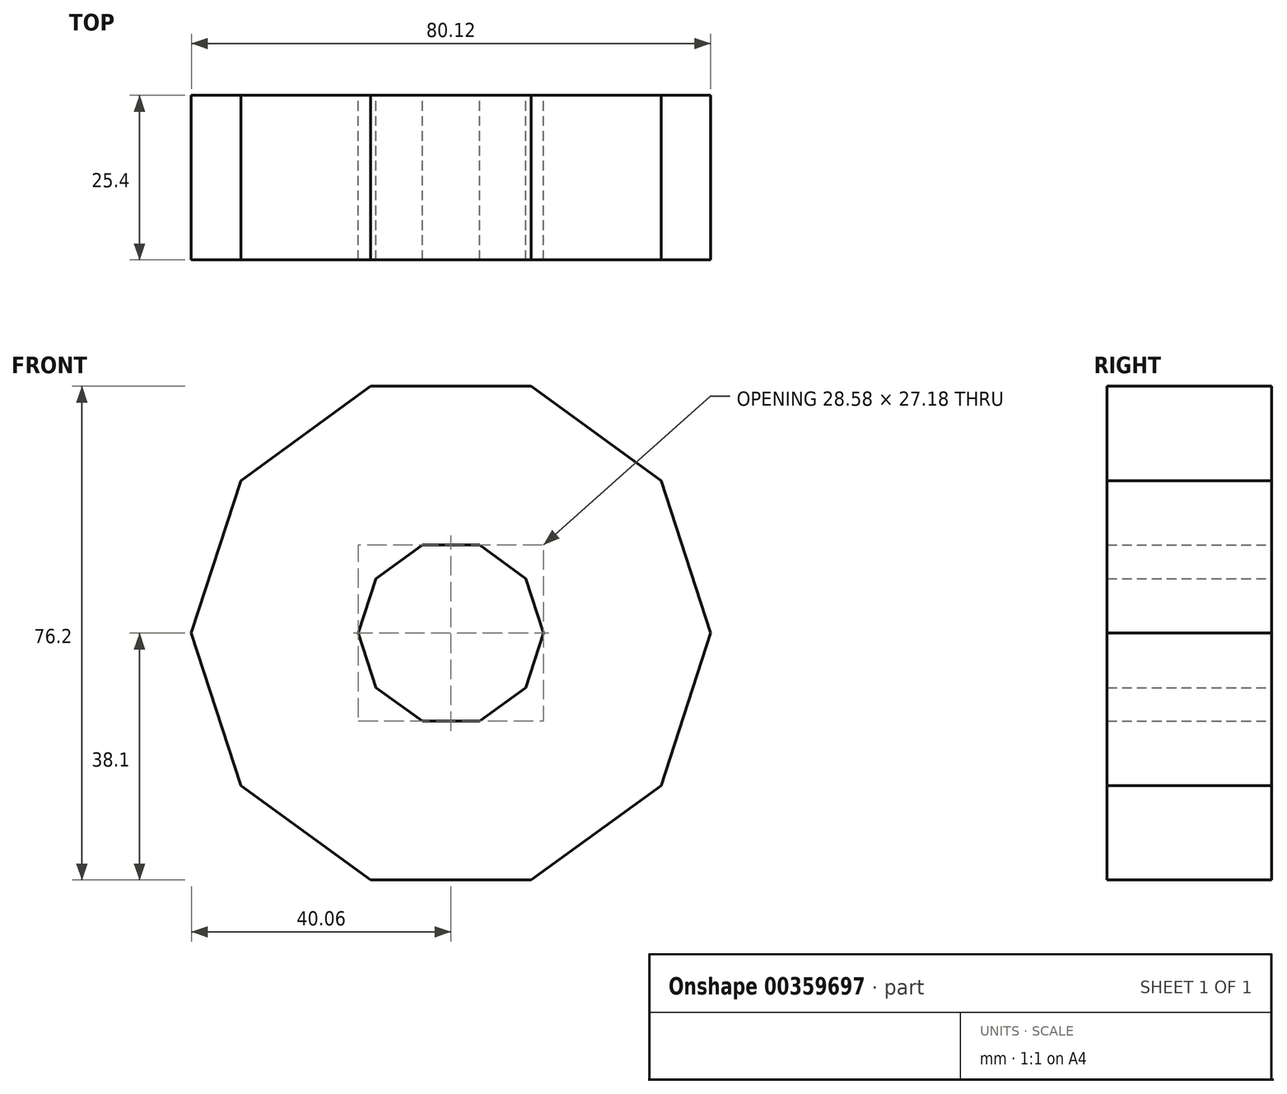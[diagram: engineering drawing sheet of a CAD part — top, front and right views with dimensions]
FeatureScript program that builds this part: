
annotation { "Feature Type Name" : "Feature", "Feature Type Description" : "" }
export const myFeature = defineFeature(function(context is Context, id is Id, definition is map)
    precondition{}
    {
        {
            var Q0;
            Q0=qCreatedBy(makeId("Front.planeOp"),FACE);
            var sketch = newSketch(context, id + "F0", { "sketchPlane" : qUnion([Q0])});
            skLineSegment(sketch, "E0", {"start": v(0, 0) * mm, "end": v(0, 38.1) * mm});
            skLineSegment(sketch, "E1", {"start": v(0, 0) * mm, "end": v(0, 13.59) * mm});
            skCircle(sketch, "E2.cCircle", {"center": v(0, 0) * mm, "radius": 38.1 * mm, "construction": true});
            skLineSegment(sketch, "E2.0", {"start": v(-12.38, 38.1) * mm, "end": v(12.38, 38.1) * mm});
            skLineSegment(sketch, "E2.1", {"start": v(12.38, 38.1) * mm, "end": v(32.4, 23.55) * mm});
            skLineSegment(sketch, "E2.2", {"start": v(32.4, 23.55) * mm, "end": v(40.06, 0) * mm});
            skLineSegment(sketch, "E2.3", {"start": v(40.06, 0) * mm, "end": v(32.4, -23.55) * mm});
            skLineSegment(sketch, "E2.4", {"start": v(32.4, -23.55) * mm, "end": v(12.38, -38.1) * mm});
            skLineSegment(sketch, "E2.5", {"start": v(12.38, -38.1) * mm, "end": v(-12.38, -38.1) * mm});
            skLineSegment(sketch, "E2.6", {"start": v(-12.38, -38.1) * mm, "end": v(-32.4, -23.55) * mm});
            skLineSegment(sketch, "E2.7", {"start": v(-32.4, -23.55) * mm, "end": v(-40.06, 0) * mm});
            skLineSegment(sketch, "E2.8", {"start": v(-40.06, 0) * mm, "end": v(-32.4, 23.55) * mm});
            skLineSegment(sketch, "E2.9", {"start": v(-32.4, 23.55) * mm, "end": v(-12.38, 38.1) * mm});
            skPoint(sketch, "E2.0.midPoint", {"position": v(0, 38.1) * mm});
            skCircle(sketch, "E3.cCircle", {"center": v(0, 0) * mm, "radius": 13.59 * mm, "construction": true});
            skLineSegment(sketch, "E3.0", {"start": v(-4.42, 13.59) * mm, "end": v(4.42, 13.59) * mm});
            skLineSegment(sketch, "E3.1", {"start": v(4.42, 13.59) * mm, "end": v(11.56, 8.4) * mm});
            skLineSegment(sketch, "E3.2", {"start": v(11.56, 8.4) * mm, "end": v(14.29, 0) * mm});
            skLineSegment(sketch, "E3.3", {"start": v(14.29, 0) * mm, "end": v(11.56, -8.4) * mm});
            skLineSegment(sketch, "E3.4", {"start": v(11.56, -8.4) * mm, "end": v(4.42, -13.59) * mm});
            skLineSegment(sketch, "E3.5", {"start": v(4.42, -13.59) * mm, "end": v(-4.42, -13.59) * mm});
            skLineSegment(sketch, "E3.6", {"start": v(-4.42, -13.59) * mm, "end": v(-11.56, -8.4) * mm});
            skLineSegment(sketch, "E3.7", {"start": v(-11.56, -8.4) * mm, "end": v(-14.29, 0) * mm});
            skLineSegment(sketch, "E3.8", {"start": v(-14.29, 0) * mm, "end": v(-11.56, 8.4) * mm});
            skLineSegment(sketch, "E3.9", {"start": v(-11.56, 8.4) * mm, "end": v(-4.42, 13.59) * mm});
            skPoint(sketch, "E3.0.midPoint", {"position": v(0, 13.59) * mm});
            skSolve(sketch);
        }
        {
            var Q0;
            {var subQ3=sQuery(id+"F0.wireOp",EDGE,"E2.1");Q0=makeQuery(id+"F0.imprint","IMPRINT",FACE,{"disambiguationData":[TD([[makeQuery(id+"F0.imprint","IMPRINT",EDGE,{"derivedFrom":subQ3}),-1.0]])]});}
            extrude(context, id + "F1", {"entities" : qUnion([Q0]), "depth" : 25.4 * mm});
        }
    });
